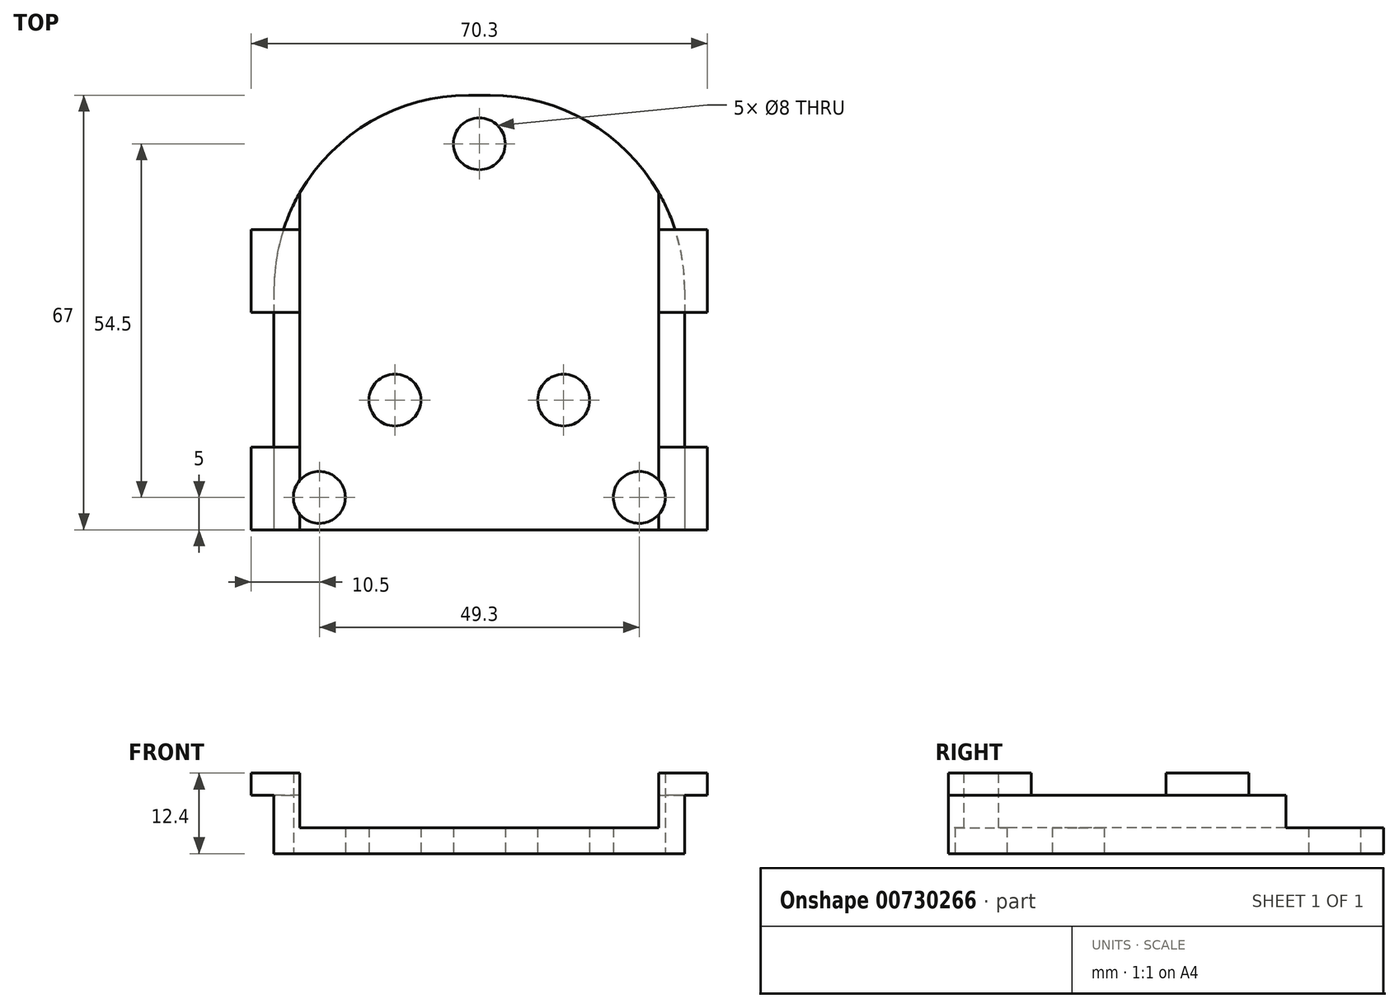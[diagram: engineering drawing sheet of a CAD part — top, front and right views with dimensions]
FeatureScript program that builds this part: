
annotation { "Feature Type Name" : "Feature", "Feature Type Description" : "" }
export const myFeature = defineFeature(function(context is Context, id is Id, definition is map)
    precondition{}
    {
        {
            var Q0;
            Q0=qCreatedBy(makeId("Top.planeOp"),FACE);
            var sketch = newSketch(context, id + "F0", { "sketchPlane" : qUnion([Q0])});
            skLineSegment(sketch, "E0.bottom", {"start": v(31.65, 33.5) * mm, "end": v(-31.65, 33.5) * mm});
            skLineSegment(sketch, "E0.top", {"start": v(31.65, -33.5) * mm, "end": v(-31.65, -33.5) * mm});
            skLineSegment(sketch, "E0.left", {"start": v(31.65, 33.5) * mm, "end": v(31.65, -33.5) * mm});
            skLineSegment(sketch, "E0.right", {"start": v(-31.65, 33.5) * mm, "end": v(-31.65, -33.5) * mm});
            skPoint(sketch, "E0.middle", {"position": v(0, 0) * mm});
            skSolve(sketch);
        }
        {
            var Q0;
            Q0=makeQuery(id+"F0.imprint","IMPRINT",FACE,{"disambiguationData":[TD([[makeQuery(id+"F0.imprint","IMPRINT",EDGE,{"derivedFrom":sQuery(id+"F0.wireOp",EDGE,"E0.bottom")}),1.0]])]});
            extrude(context, id + "F1", {"entities" : qUnion([Q0]), "depth" : 4 * mm, "offsetDistance" : 25 * mm});
        }
        {
            var Q0;
            Q0=qCreatedBy(makeId("Top.planeOp"),FACE);
            var sketch = newSketch(context, id + "F2", { "sketchPlane" : qUnion([Q0])});
            skCircle(sketch, "E1", {"center": v(-24.65, -28.5) * mm, "radius": 4 * mm});
            skCircle(sketch, "E2", {"center": v(24.65, -28.5) * mm, "radius": 4 * mm});
            skSolve(sketch);
        }
        {
            var Q0;
            Q0=makeQuery(id+"F1.opExtrude","CAP_FACE",FACE,{"disambiguationData":[OSD([sQuery(id+"F0.wireOp",EDGE,"E0.bottom"),sQuery(id+"F0.wireOp",EDGE,"E0.top"),sQuery(id+"F0.wireOp",EDGE,"E0.left"),sQuery(id+"F0.wireOp",EDGE,"E0.right")])],"isStart":false});
            var sketch = newSketch(context, id + "F3", { "sketchPlane" : qUnion([Q0])});
            skLineSegment(sketch, "E3.bottom", {"start": v(-31.65, 33.5) * mm, "end": v(-27.65, 33.5) * mm});
            skLineSegment(sketch, "E3.top", {"start": v(-31.65, -33.5) * mm, "end": v(-27.65, -33.5) * mm});
            skLineSegment(sketch, "E3.left", {"start": v(-31.65, 33.5) * mm, "end": v(-31.65, -33.5) * mm});
            skLineSegment(sketch, "E3.right", {"start": v(-27.65, 33.5) * mm, "end": v(-27.65, -33.5) * mm});
            skLineSegment(sketch, "E4.bottom", {"start": v(27.65, 33.5) * mm, "end": v(31.65, 33.5) * mm});
            skLineSegment(sketch, "E4.top", {"start": v(27.65, -33.5) * mm, "end": v(31.65, -33.5) * mm});
            skLineSegment(sketch, "E4.left", {"start": v(27.65, 33.5) * mm, "end": v(27.65, -33.5) * mm});
            skLineSegment(sketch, "E4.right", {"start": v(31.65, 33.5) * mm, "end": v(31.65, -33.5) * mm});
            skSolve(sketch);
        }
        {
            var Q0;
            Q0 = qSketchRegion(id + "F3", true);
            extrude(context, id + "F4", {"entities" : qUnion([Q0]), "operationType" : NewBodyOperationType.ADD, "depth" : 5 * mm, "offsetDistance" : 25 * mm});
        }
        {
            var Q0;
            Q0=makeQuery(id+"F4.opExtrude","CAP_FACE",FACE,{"disambiguationData":[OSD([sQuery(id+"F3.wireOp",EDGE,"E3.bottom"),sQuery(id+"F3.wireOp",EDGE,"E3.top"),sQuery(id+"F3.wireOp",EDGE,"E3.left"),sQuery(id+"F3.wireOp",EDGE,"E3.right")])],"isStart":false});
            var sketch = newSketch(context, id + "F5", { "sketchPlane" : qUnion([Q0])});
            skLineSegment(sketch, "E5.bottom", {"start": v(-31.65, -20.75) * mm, "end": v(-27.65, -20.75) * mm});
            skLineSegment(sketch, "E5.top", {"start": v(-31.65, -33.5) * mm, "end": v(-27.65, -33.5) * mm});
            skLineSegment(sketch, "E5.left", {"start": v(-31.65, -20.75) * mm, "end": v(-31.65, -33.5) * mm});
            skLineSegment(sketch, "E5.right", {"start": v(-27.65, -20.75) * mm, "end": v(-27.65, -33.5) * mm});
            skLineSegment(sketch, "E6.bottom", {"start": v(-31.65, 12.75) * mm, "end": v(-27.65, 12.75) * mm});
            skLineSegment(sketch, "E6.top", {"start": v(-31.65, 0) * mm, "end": v(-27.65, 0) * mm});
            skLineSegment(sketch, "E6.left", {"start": v(-31.65, 12.75) * mm, "end": v(-31.65, 0) * mm});
            skLineSegment(sketch, "E6.right", {"start": v(-27.65, 12.75) * mm, "end": v(-27.65, 0) * mm});
            skLineSegment(sketch, "E7.bottom", {"start": v(27.65, -20.75) * mm, "end": v(31.66, -20.75) * mm});
            skLineSegment(sketch, "E7.top", {"start": v(27.65, -33.5) * mm, "end": v(31.66, -33.5) * mm});
            skLineSegment(sketch, "E7.left", {"start": v(27.65, -20.75) * mm, "end": v(27.65, -33.5) * mm});
            skLineSegment(sketch, "E7.right", {"start": v(31.66, -20.75) * mm, "end": v(31.66, -33.5) * mm});
            skLineSegment(sketch, "E8.bottom", {"start": v(27.65, 12.75) * mm, "end": v(31.76, 12.75) * mm});
            skLineSegment(sketch, "E8.top", {"start": v(27.65, 0) * mm, "end": v(31.76, 0) * mm});
            skLineSegment(sketch, "E8.left", {"start": v(27.65, 12.75) * mm, "end": v(27.65, 0) * mm});
            skLineSegment(sketch, "E8.right", {"start": v(31.76, 12.75) * mm, "end": v(31.76, 0) * mm});
            skSolve(sketch);
        }
        {
            var Q0;
            Q0=makeQuery(id+"F5.imprint","IMPRINT",FACE,{"disambiguationData":[TD([[makeQuery(id+"F5.imprint","IMPRINT",EDGE,{"derivedFrom":sQuery(id+"F5.wireOp",EDGE,"E6.bottom")}),-1.0]])]});
            var sketch = newSketch(context, id + "F6", { "sketchPlane" : qUnion([Q0])});
            skLineSegment(sketch, "E9.bottom", {"start": v(-27.65, 0) * mm, "end": v(-35.15, 0) * mm});
            skLineSegment(sketch, "E9.top", {"start": v(-27.65, 12.75) * mm, "end": v(-35.15, 12.75) * mm});
            skLineSegment(sketch, "E9.left", {"start": v(-27.65, 0) * mm, "end": v(-27.65, 12.75) * mm});
            skLineSegment(sketch, "E9.right", {"start": v(-35.15, 0) * mm, "end": v(-35.15, 12.75) * mm});
            skLineSegment(sketch, "E10.bottom", {"start": v(-27.65, -33.5) * mm, "end": v(-35.15, -33.5) * mm});
            skLineSegment(sketch, "E10.top", {"start": v(-27.65, -20.75) * mm, "end": v(-35.15, -20.75) * mm});
            skLineSegment(sketch, "E10.left", {"start": v(-27.65, -33.5) * mm, "end": v(-27.65, -20.75) * mm});
            skLineSegment(sketch, "E10.right", {"start": v(-35.15, -33.5) * mm, "end": v(-35.15, -20.75) * mm});
            skLineSegment(sketch, "E11.bottom", {"start": v(27.65, -20.75) * mm, "end": v(35.15, -20.75) * mm});
            skLineSegment(sketch, "E11.top", {"start": v(27.65, -33.5) * mm, "end": v(35.15, -33.5) * mm});
            skLineSegment(sketch, "E11.left", {"start": v(27.65, -20.75) * mm, "end": v(27.65, -33.5) * mm});
            skLineSegment(sketch, "E11.right", {"start": v(35.15, -20.75) * mm, "end": v(35.15, -33.5) * mm});
            skLineSegment(sketch, "E12.bottom", {"start": v(27.65, 12.75) * mm, "end": v(35.15, 12.75) * mm});
            skLineSegment(sketch, "E12.top", {"start": v(27.65, 0) * mm, "end": v(35.15, 0) * mm});
            skLineSegment(sketch, "E12.left", {"start": v(27.65, 12.75) * mm, "end": v(27.65, 0) * mm});
            skLineSegment(sketch, "E12.right", {"start": v(35.15, 12.75) * mm, "end": v(35.15, 0) * mm});
            skSolve(sketch);
        }
        {
            var Q0;
            Q0 = qSketchRegion(id + "F6", true);
            extrude(context, id + "F7", {"entities" : qUnion([Q0]), "operationType" : NewBodyOperationType.ADD, "depth" : 3.4 * mm, "offsetDistance" : 25 * mm});
        }
        {
            var Q0;
            Q0=qCreatedBy(makeId("Top.planeOp"),FACE);
            var sketch = newSketch(context, id + "F8", { "sketchPlane" : qUnion([Q0])});
            skCircle(sketch, "E13", {"center": v(0, 26) * mm, "radius": 4 * mm});
            skCircle(sketch, "E14", {"center": v(-13, -13.5) * mm, "radius": 4 * mm});
            skCircle(sketch, "E15", {"center": v(13, -13.5) * mm, "radius": 4 * mm});
            skSolve(sketch);
        }
        {
            var Q0;
            Q0 = qSketchRegion(id + "F2", true);
            extrude(context, id + "F9", {"entities" : qUnion([Q0]), "operationType" : NewBodyOperationType.REMOVE, "depth" : 25 * mm, "offsetDistance" : 25 * mm});
        }
        {
            var Q0;
            Q0 = qSketchRegion(id + "F8", true);
            extrude(context, id + "F10", {"entities" : qUnion([Q0]), "operationType" : NewBodyOperationType.REMOVE, "depth" : 25 * mm, "offsetDistance" : 25 * mm});
        }
        {
            var Q0;
            Q0=makeQuery(id+"F4.boolean.opBoolean","MERGE",EDGE,{"derivedFrom":[makeQuery(id+"F1.opExtrude","SWEPT_EDGE",EDGE,{"disambiguationData":[OSD([sQuery(id+"F0.wireOp",EDGE,"E0.bottom"),sQuery(id+"F0.wireOp",EDGE,"E0.right")])]}),makeQuery(id+"F4.opExtrude","SWEPT_EDGE",EDGE,{"disambiguationData":[OSD([sQuery(id+"F3.wireOp",EDGE,"E3.bottom"),sQuery(id+"F3.wireOp",EDGE,"E3.left")])]})]});
            fillet(context, id + "F11", {"entities" : qUnion([Q0]), "tangentPropagation" : true, "radius" : 30 * mm, "defaultsChanged" : true, "vertexSettings" : [], "allowEdgeOverflow" : false});
        }
        {
            var Q0;
            Q0=makeQuery(id+"F4.boolean.opBoolean","MERGE",EDGE,{"derivedFrom":[makeQuery(id+"F1.opExtrude","SWEPT_EDGE",EDGE,{"disambiguationData":[OSD([sQuery(id+"F0.wireOp",EDGE,"E0.bottom"),sQuery(id+"F0.wireOp",EDGE,"E0.left")])]}),makeQuery(id+"F4.opExtrude","SWEPT_EDGE",EDGE,{"disambiguationData":[OSD([sQuery(id+"F3.wireOp",EDGE,"E4.bottom"),sQuery(id+"F3.wireOp",EDGE,"E4.right")])]})]});
            fillet(context, id + "F12", {"entities" : qUnion([Q0]), "tangentPropagation" : true, "radius" : 30 * mm, "defaultsChanged" : true, "vertexSettings" : [], "allowEdgeOverflow" : false});
        }
    });
